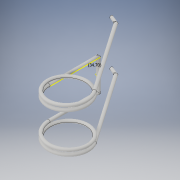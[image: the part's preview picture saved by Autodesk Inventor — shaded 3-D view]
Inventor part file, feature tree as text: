
AUTODESK INVENTOR PART (.ipt)
format: ipt  version: 2018 (Build 220112000, 112)  size: 277,504 bytes
history: native  units: in
note: dims shown in document units (in); Inventor stores cm internally (conversion verified against a paired STEP export)
features: sketch x11, extrude x7, projected_geometry x6, mirror x3, fillet x2, helix x1, plane x1, sweep x1
ambient origin geometry x8: Origin, YZ Plane, XZ Plane, XY Plane, X Axis, Y Axis, Z Axis, Center Point
bodies: Solid1 (feature_tree)
feature tree (32):
  helix  "Coil1"  [1 undecoded]
  extrude  "Extrusion1"  Depth=0.95in TaperAngle=0.0deg
  extrude  "Extrusion2"  Depth=0.0175in
  extrude  "Extrusion3"  Depth=0.035in
  extrude  "Extrusion4"  Depth=0.1925in TaperAngle=0.0deg
  extrude  "Extrusion5"  Depth=0.1in
  plane  "Work Plane1"
  mirror  "Mirror1"
  sweep  "Sweep1"
  fillet  "Fillet1"  [1 undecoded]
  extrude  "Extrusion6"  Depth=0.035in
  mirror  "Mirror2"
  fillet  "Fillet2"  Radius=0.2385in
  mirror  "Mirror3"
  sketch  "Sketch10"
  extrude  "Extrusion7"  Depth=1.0in TaperAngle=0.0deg
  sketch  "Sketch1"  dims[d1=0.215in]
  sketch  "Sketch2"  dims[d2=0.075in d3=0.075in d4=0.6285in d5=0.0in d6=90.0deg d7=90.0deg d8=0.0in d9=0.0in d10=0.95in d11=0.0in]
  projected_geometry  "Projected Loop1"
  sketch  "Sketch3"  dims[d12=0.575in d13=0.0in d14=0.0175in]
  sketch  "Sketch4"  dims[d15=0.175in d16=0.0in d17=0.035in]
  projected_geometry  "Projected Loop2"
  sketch  "Sketch5"  dims[d18=0.1925in d19=0.0in d20=0.1925in d21=0.0in]
  projected_geometry  "Projected Loop3"
  sketch  "Sketch6"  dims[d22=0.0in d23=0.1in]
  projected_geometry  "Projected Loop4"
  sketch  "Sketch7"  dims[d25=0.0in d26=0.0in d27=0.035in d28=45.0deg]
  projected_geometry  "Projected Loop5"
  sketch  "Sketch8"  dims[d29=0.1925in d30=0.0in d31=0.035in d32=0.2385in]
  projected_geometry  "Projected Loop6"
  sketch  "Sketch9"  dims[d33=0.2268in d34=1.0in d35=0.0in]
  sketch  "Sketch11"
note: 2 required parameter values undecoded (feature->parameter linkage not recoverable at this tier; creation-order binding heuristic only, values carry confidence <= 0.55)
